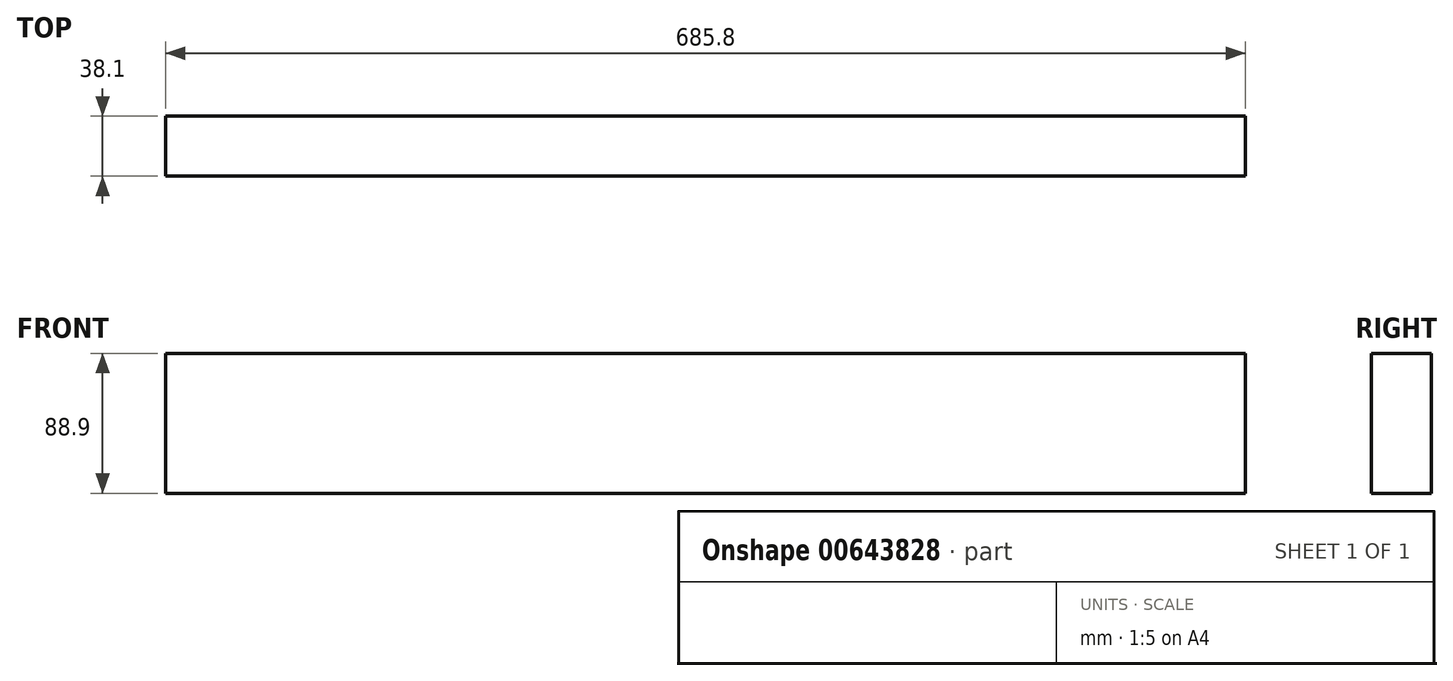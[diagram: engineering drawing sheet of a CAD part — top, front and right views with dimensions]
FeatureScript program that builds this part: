
annotation { "Feature Type Name" : "Feature", "Feature Type Description" : "" }
export const myFeature = defineFeature(function(context is Context, id is Id, definition is map)
    precondition{}
    {
        {
            var Q0;
            Q0=qCreatedBy(makeId("Front.planeOp"),FACE);
            var sketch = newSketch(context, id + "F0", { "sketchPlane" : qUnion([Q0])});
            skLineSegment(sketch, "E0.bottom", {"start": v(519.6, 1.18) * mm, "end": v(-166.2, 1.18) * mm});
            skLineSegment(sketch, "E0.top", {"start": v(519.6, 90.08) * mm, "end": v(-166.2, 90.08) * mm});
            skLineSegment(sketch, "E0.left", {"start": v(519.6, 1.18) * mm, "end": v(519.6, 90.08) * mm});
            skLineSegment(sketch, "E0.right", {"start": v(-166.2, 1.18) * mm, "end": v(-166.2, 90.08) * mm});
            skPoint(sketch, "E0.middle", {"position": v(176.7, 45.63) * mm});
            skSolve(sketch);
        }
        {
            var Q0;
            Q0 = qSketchRegion(id + "F0", true);
            extrude(context, id + "F1", {"entities" : qUnion([Q0]), "depth" : 38.1 * mm, "offsetDistance" : 25.4 * mm});
        }
    });
